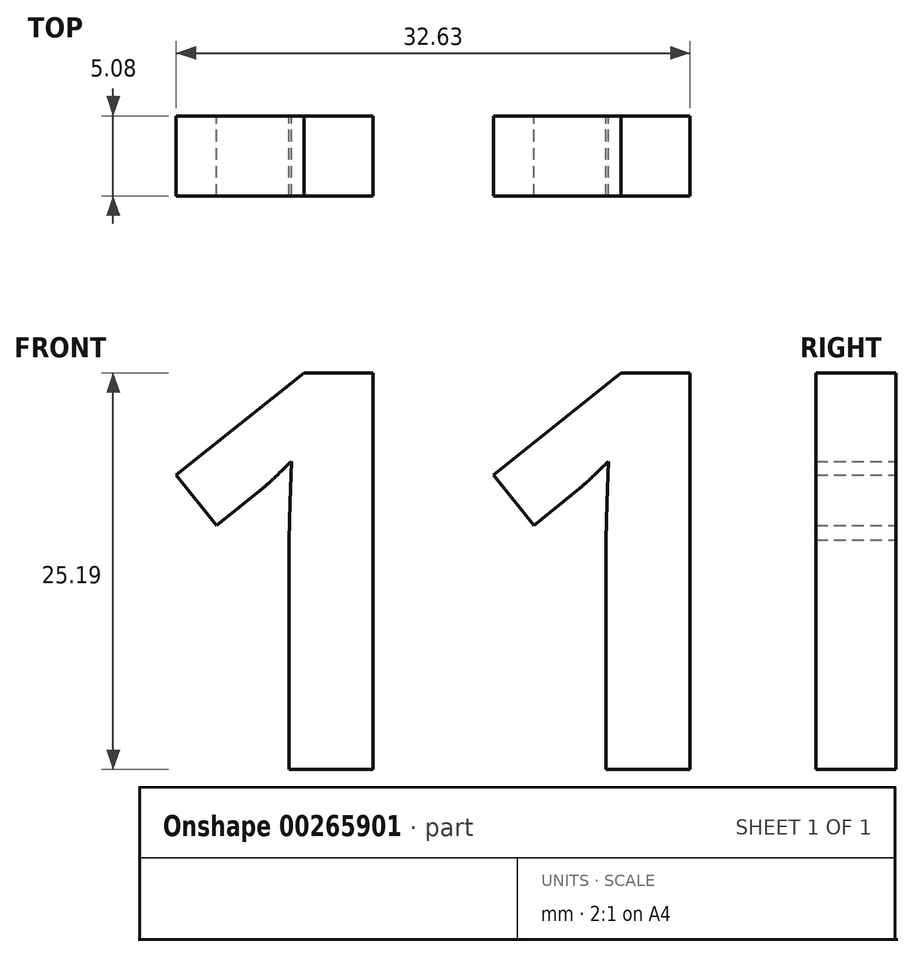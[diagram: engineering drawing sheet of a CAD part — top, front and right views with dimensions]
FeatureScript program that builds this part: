
annotation { "Feature Type Name" : "Feature", "Feature Type Description" : "" }
export const myFeature = defineFeature(function(context is Context, id is Id, definition is map)
    precondition{}
    {
        {
            var Q0;
            Q0=qCreatedBy(makeId("Front.planeOp"),FACE);
            var sketch = newSketch(context, id + "F0", { "sketchPlane" : qUnion([Q0])});
            skText(sketch, "E0", { "text": "11", "fontName": "OpenSans-Bold.ttf"});
            const initialGuessF0  = {"E0": [-0.07091, 0.00564, 1, 0, 0.0254]};
            skSetInitialGuess(sketch, initialGuessF0);
            skSolve(sketch);
        }
        {
            var Q0;
            Q0 = qSketchRegion(id + "F0", true);
            extrude(context, id + "F1", {"entities" : qUnion([Q0]), "depth" : 5.08 * mm});
        }
    });
